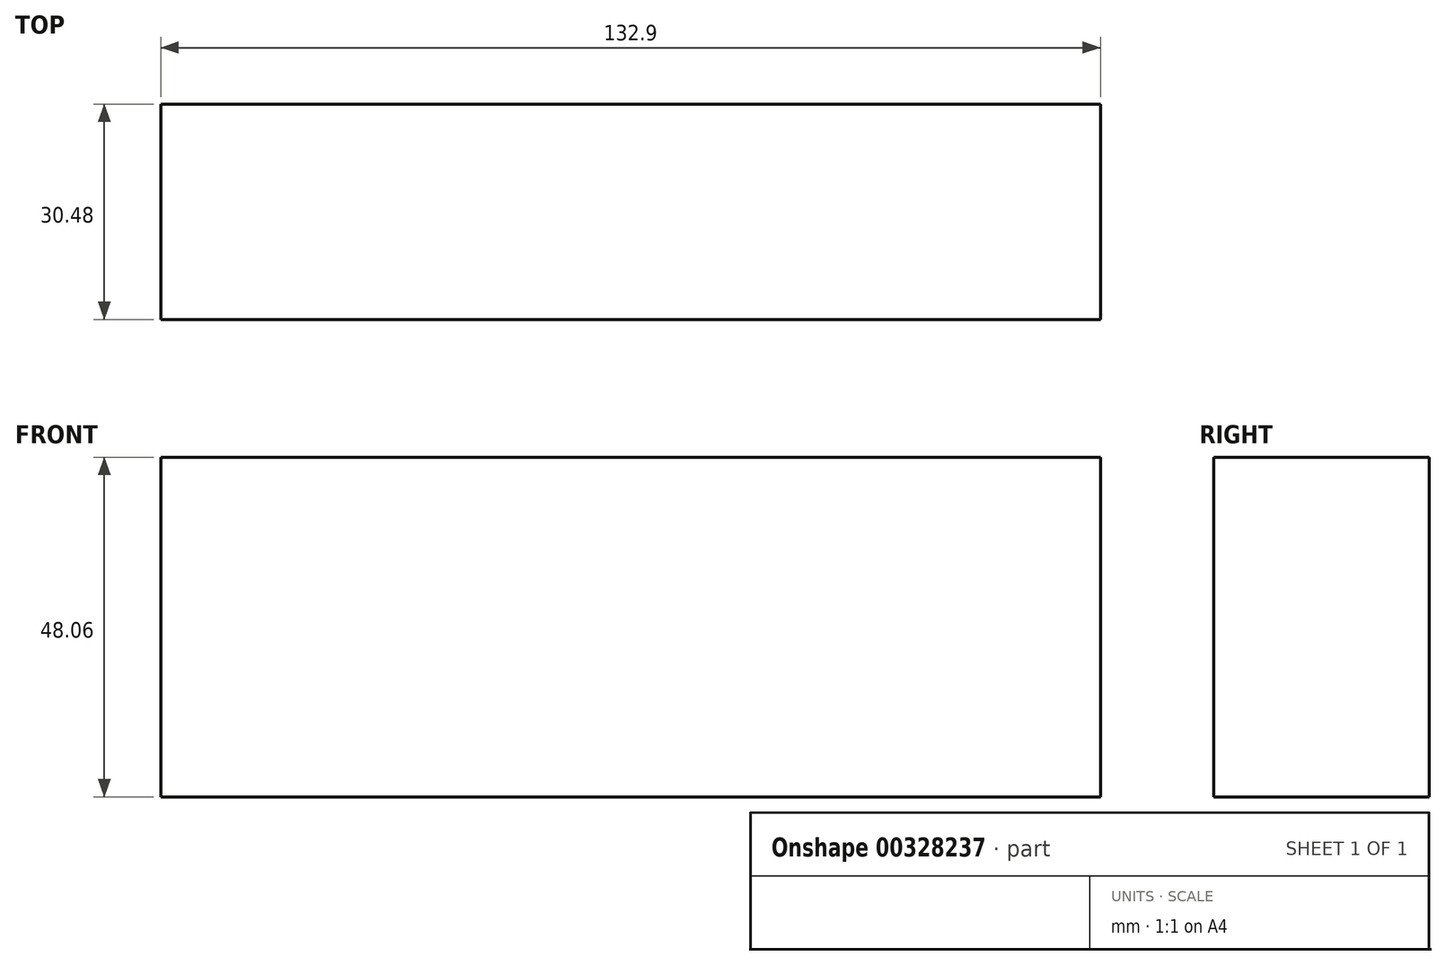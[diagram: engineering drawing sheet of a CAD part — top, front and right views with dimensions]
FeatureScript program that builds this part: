
annotation { "Feature Type Name" : "Feature", "Feature Type Description" : "" }
export const myFeature = defineFeature(function(context is Context, id is Id, definition is map)
    precondition{}
    {
        {
            var Q0;
            Q0=qCreatedBy(makeId("Front.planeOp"),FACE);
            var sketch = newSketch(context, id + "F0", { "sketchPlane" : qUnion([Q0])});
            skLineSegment(sketch, "E0.bottom", {"start": v(-87.93, 30.34) * mm, "end": v(44.97, 30.34) * mm});
            skLineSegment(sketch, "E0.top", {"start": v(-87.93, -17.72) * mm, "end": v(44.97, -17.72) * mm});
            skLineSegment(sketch, "E0.left", {"start": v(-87.93, 30.34) * mm, "end": v(-87.93, -17.72) * mm});
            skLineSegment(sketch, "E0.right", {"start": v(44.97, 30.34) * mm, "end": v(44.97, -17.72) * mm});
            skSolve(sketch);
        }
        {
            var Q0;
            Q0=makeQuery(id+"F0.imprint","IMPRINT",FACE,{"disambiguationData":[TD([[makeQuery(id+"F0.imprint","IMPRINT",EDGE,{"derivedFrom":sQuery(id+"F0.wireOp",EDGE,"E0.bottom")}),-1.0]])]});
            extrude(context, id + "F1", {"entities" : qUnion([Q0]), "depth" : 30.48 * mm});
        }
    });
